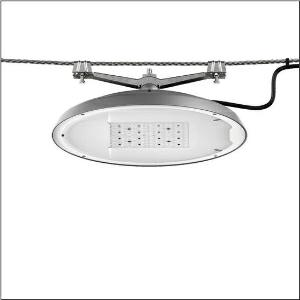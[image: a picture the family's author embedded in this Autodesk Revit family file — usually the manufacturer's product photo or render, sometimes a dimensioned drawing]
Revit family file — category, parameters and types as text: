
# Revit family: dl_r__50_iq_mini___st1_0s_5xa248w31f08me_86a1
name_source: partatom
category: Lighting Fixtures
units: mm (PartAtom-declared; Revit-internal decimal feet)

## family parameters
Cut with Voids When Loaded = No
Host = Face
Light Source = No
Part Type = Normal
Room Calculation Point = No
Round Connector Dimension = Use Diameter
Shared = No

## types (1)
- --- (1 x LED, 15660 lm, 107.8 W, 3000K)
    Apparent Load = 108 VA
    CIE Flux Codes = 37 72 97 100 100
    Color Rendering = 70
    Color Temperature = 3000K
    Default Elevation = 1800 mm
    Description = DL® 50 iQ mini, catenary luminaire, primary light control with lens, of PMMA, primary optical cover: cover, of toughened safety glass, transparent, light distribution: ST1.0s, light emission: direct distribution, primary light characteristic: symmetric, installation type: suspended mounting, LED, High Power LED, rated luminous flux: 15.660lm, luminous efficacy: 145lm/W, light colour: 730, colour temperature: 3000K, control: optimised constant luminous flux control (CLO 2.0), Desk-Remote (wireless, voltage-free reading and setting of iQ features in the workshop via application-optimized NFC function/RFID function), Light-Fading, Smart-Wire, Night-Set, Lumen-Switch, Temp-Guard, Auto-Match, Street-Remote, mains connection: 230..240V, AC, 50/60Hz, start of lifetime: 108W, end of service life: 118W, reduction: 47W, luminaire housing, of diecast aluminium, powder-coated, Siteco® metallic grey (DB 702S), diameter: 500mm, height: 115mm, protection rating (complete): IP66, insulation class (complete): insulation class II (safety insulation), certification: CE, ENEC, VDE, impact resistance: IK08, permissible operating ambient temperature for outdoor applications: -25..+40°C, standard-compliant lighting for roads and squares, packaging unit: 1 piece

Light Distribution: ST1.0s
    Height = 124 mm  [stored 0.406824 ft]
    Lamp = 1 x LED
    Lamp Light Flux = 15660 lm
    Lamp Power = 107.8 W
    Lamp count = 1
    Length = 500 mm
    Luminous efficacy = 145 lm/W
    Manufacturer = Siteco
    ModVariant = No
    Model = 5XA248W31F08ME
    Number of Poles = 1
    OnlyDefault = Yes
    Power Factor = 1
    Product Name = DL® 50 iQ mini | ST1.0s
    Product group = catenary luminaire
    ProductGroupID = 6300
    Protection Class = Protection class II
    Protection Degree = IP 66
    RLX_Detail_Level = 1
    RLX_Emergency_Light_Flux = 0 lm
    RLX_Emergency_Type = 0
    RLX_Emergency_Type_DB = No
    RlxData = <blob elided: 127041 chars, md5=d6eba5eb>
    Socket = socket
    Standby Power = 0 W
    System Light Flux = 15660 lm
    System Power = 108 W
    Type Comments = factory setting: luminous flux: 100 % | dim-lin: 254 | 565 mA
    Type Image = l_1251783.jpg
    URL = http://relux.com
    VarID = @adj_089781
    Voltage = 0 V
    Weight = 0.00 kg
    Width = 0 mm  [stored 0 ft]

note: [stored X ft] marks values corroborated as IEEE doubles in the binary element streams (Revit-internal decimal feet)

## geometry (parser evidence)
native form markers: Blend x4, Sweep x14
no freeform markers — native parametric forms only
